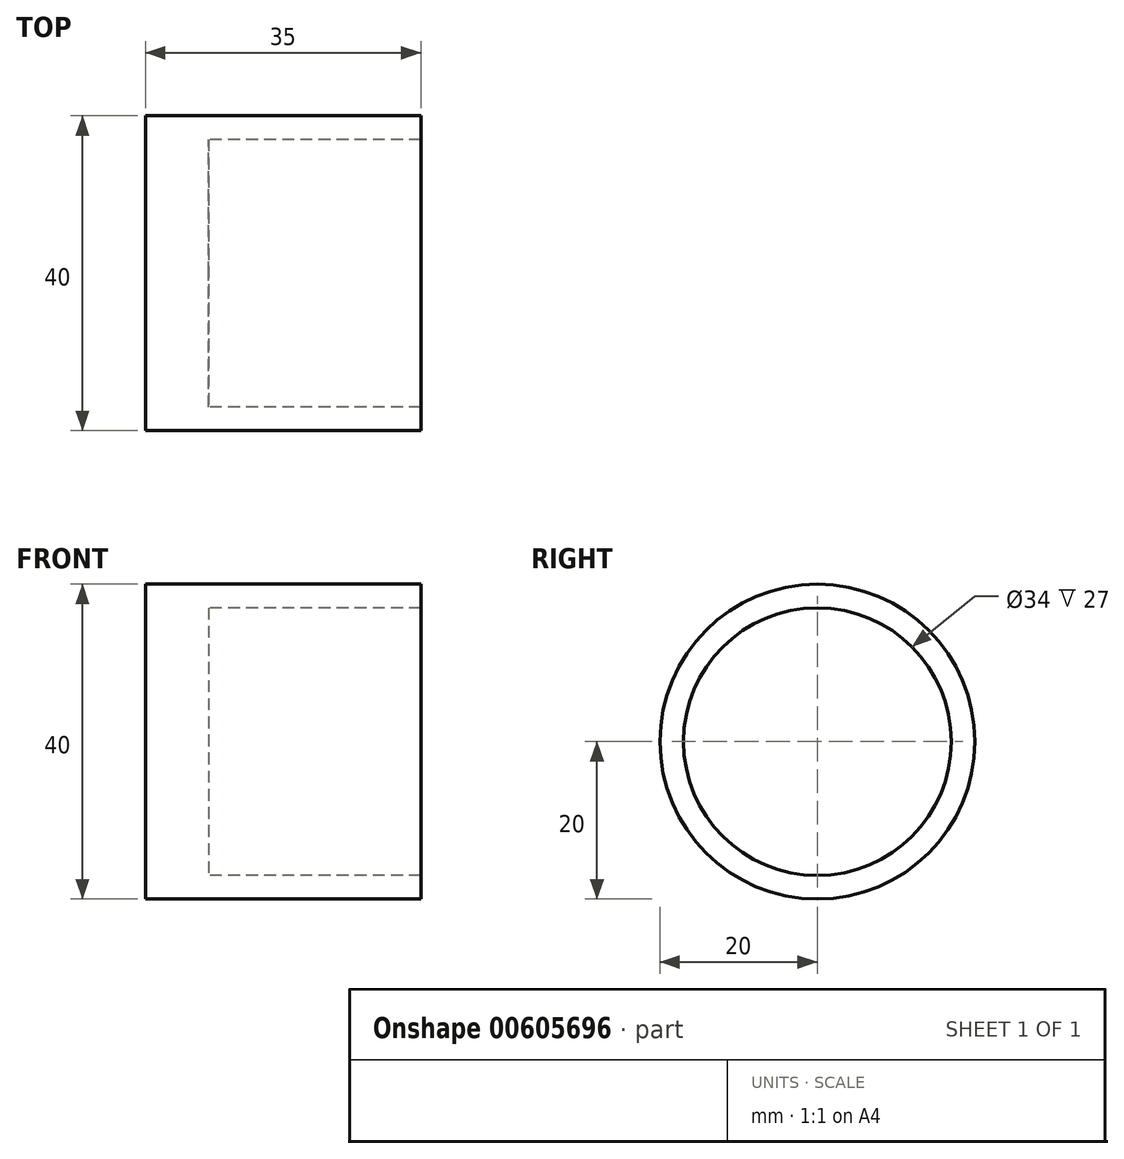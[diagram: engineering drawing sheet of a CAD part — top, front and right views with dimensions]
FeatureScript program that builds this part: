
annotation { "Feature Type Name" : "Feature", "Feature Type Description" : "" }
export const myFeature = defineFeature(function(context is Context, id is Id, definition is map)
    precondition{}
    {
        {
            var Q0;
            Q0=qCreatedBy(makeId("Front.planeOp"),FACE);
            var sketch = newSketch(context, id + "F0", { "sketchPlane" : qUnion([Q0])});
            skLineSegment(sketch, "E0", {"start": v(0, 0) * mm, "end": v(0, 20) * mm});
            skLineSegment(sketch, "E1", {"start": v(0, 20) * mm, "end": v(35, 20) * mm});
            skLineSegment(sketch, "E2", {"start": v(35, 20) * mm, "end": v(35, 17) * mm});
            skLineSegment(sketch, "E3", {"start": v(35, 17) * mm, "end": v(8, 17) * mm});
            skLineSegment(sketch, "E4", {"start": v(8, 17) * mm, "end": v(8, 0) * mm});
            skLineSegment(sketch, "E5", {"start": v(8, 0) * mm, "end": v(0, 0) * mm});
            skLineSegment(sketch, "E6", {"start": v(-32.44, 0) * mm, "end": v(70.52, 0) * mm});
            skSolve(sketch);
        }
        {
            var Q0;
            {var subQ0=sQuery(id+"F0.wireOp",EDGE,"E0");Q0=makeQuery(id+"F0.imprint","IMPRINT",FACE,{"disambiguationData":[TD([[makeQuery(id+"F0.imprint","IMPRINT",EDGE,{"derivedFrom":subQ0}),-1.0]])]});}
            var Q1;
            Q1=sQuery(id+"F0.wireOp",EDGE,"E6");
            revolve(context, id + "F1", {"entities" : qUnion([Q0]), "axis" : qUnion([Q1]), "revolveType" : RevolveType.FULL});
        }
    });
